# Revit family: Ray 17_ Pendant
name_source: partatom
category: Lighting Fixtures
revit_build: Autodesk Revit 2017 (Build: 20190508_0315(x64)
units: mm (PartAtom-declared; Revit-internal decimal feet)

## family parameters
Cut with Voids When Loaded = No
Host = Face
Light Source = Yes
Part Type = Normal
Room Calculation Point = No
Round Connector Dimension = Use Diameter
Shared = No

## types (1)
- Ray 17_ Pendant
    Canopy Width = 5"
    Color Filter = 16777215
    Cost = 774 $
    Default Elevation = 0"
    Description = Inspired by the playful yet sophisticated spirit present in all of Ray Eames' collections, this iconic pendant puts a modern twist on a classic mid-century design. A homage to the rich color palette of the 1960s, an assortment of elegantly elevated primary hues brighten the room even when unlit. Each fixture is constructed with a steel spun shade in muted finishes and paired with a glass diffuser to gently filter light. Assembled in our Portland, Ore. factory using ethically-sourced domestic and global components. A Schoolhouse Original.
    Dimming Lamp Color Temperature Shift = <None>
    Height = 18"
    Light Source Symbol Length = 8 1/2"
    Max Wattage = 40 W
    Primary Finishes = Dune, White, Paprika, Black, Pool Blue
    Product Material = Steel
    Spot Beam Angle = 30.00°
    Spot Field Angle = 90.00°
    Tilt Angle = 60.00°
    URL = https://www.schoolhouse.com
    Voltage = 120/220 V
    Width = 17"

## geometry (parser evidence)
native form markers: Sweep x5
no freeform markers — native parametric forms only
